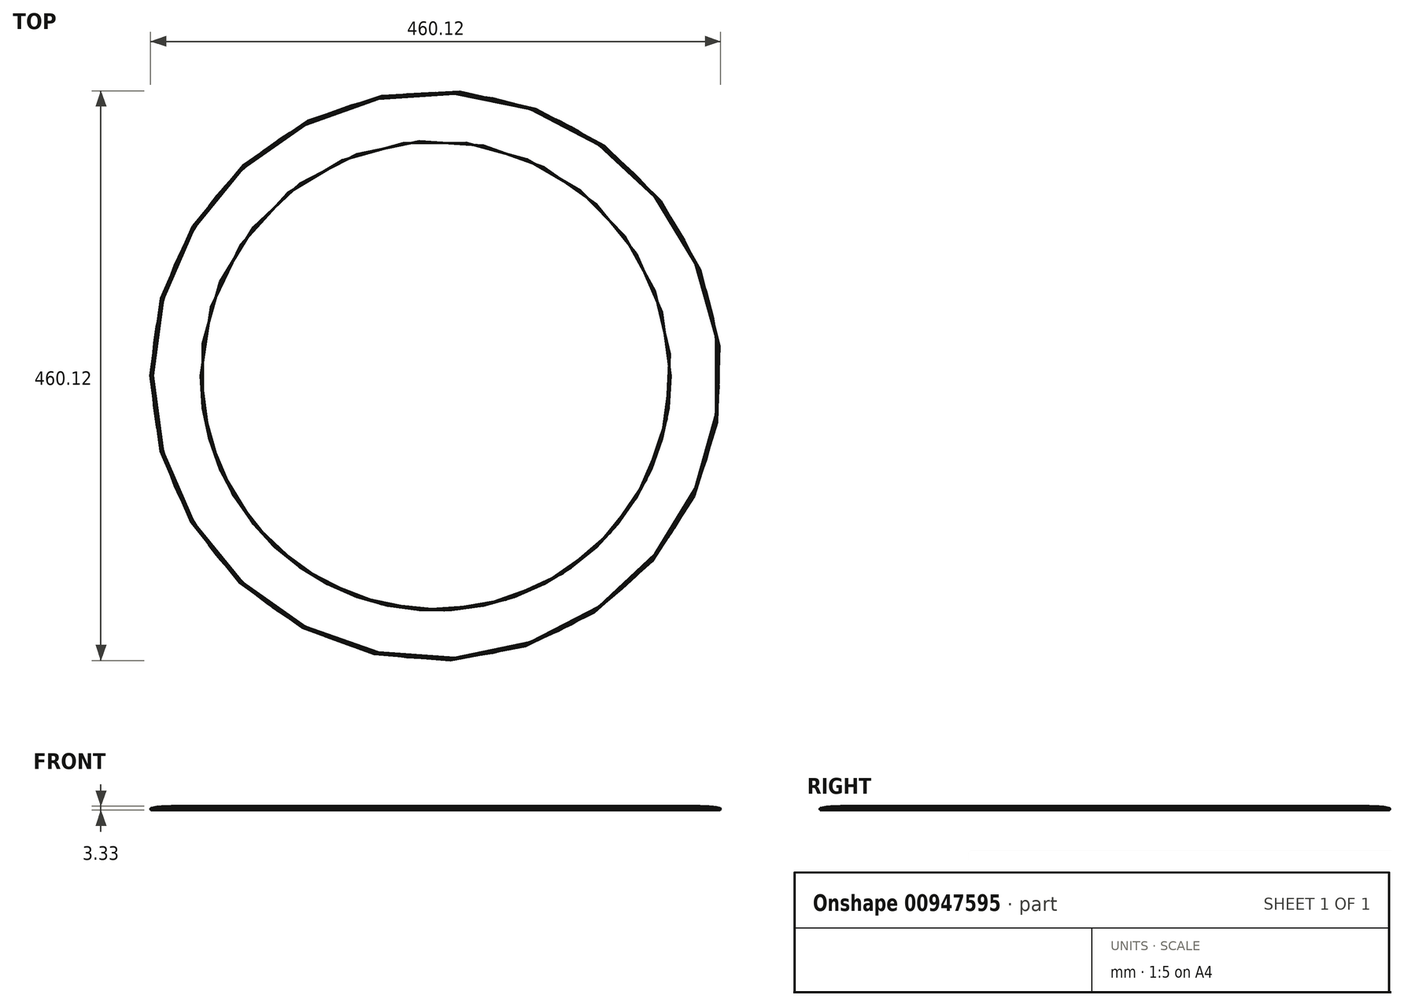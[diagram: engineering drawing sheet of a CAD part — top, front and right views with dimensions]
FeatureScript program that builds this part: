
annotation { "Feature Type Name" : "Feature", "Feature Type Description" : "" }
export const myFeature = defineFeature(function(context is Context, id is Id, definition is map)
    precondition{}
    {
        {
            var Q0;
            Q0=qCreatedBy(makeId("Front.planeOp"),FACE);
            var sketch = newSketch(context, id + "F0", { "sketchPlane" : qUnion([Q0])});
            skLineSegment(sketch, "E0", {"start": v(0, 0) * mm, "end": v(0, 158.75) * mm, "construction": true});
            skLineSegment(sketch, "E1", {"start": v(0, 0) * mm, "end": v(228.6, 0) * mm, "construction": true});
            skLineSegment(sketch, "E2", {"start": v(0, 158.75) * mm, "end": v(44.45, 158.75) * mm, "construction": true});
            skLineSegment(sketch, "E3", {"start": v(44.45, 158.75) * mm, "end": v(44.45, 143.35) * mm, "construction": true});
            skLineSegment(sketch, "E4", {"start": v(44.45, 158.75) * mm, "end": v(86, 158.75) * mm, "construction": true});
            skFitSpline(sketch, "E5", {"points": [v(86, 158.75) * mm, v(63.64, 148.01) * mm, v(44.45, 120.75) * mm, v(41.2, 74.17) * mm, v(59.88, 37.7) * mm, v(85.33, 18.53) * mm, v(127.5, 6.62) * mm, v(179.12, 3.65) * mm, v(188.03, 3.3) * mm, v(189.18, 2.94) * mm, v(189.55, 2.35) * mm, v(189.64, 2) * mm, v(188.74, 0) * mm], "startDerivative": vector(-219.08, -34.84) * mm, "endDerivative": vector(-71.32, -16.42) * mm});
            skPoint(sketch, "E6", {"position": v(65.23, 158.75) * mm});
            skFitSpline(sketch, "E7.MirrorCS", {"points": [v(-86, 158.75) * mm, v(-63.64, 148.01) * mm, v(-44.45, 120.75) * mm, v(-41.2, 74.17) * mm, v(-59.88, 37.7) * mm, v(-85.33, 18.53) * mm, v(-127.5, 6.62) * mm, v(-179.12, 3.65) * mm, v(-188.03, 3.3) * mm, v(-189.18, 2.94) * mm, v(-189.55, 2.35) * mm, v(-189.64, 2) * mm, v(-188.74, 0) * mm], "startDerivative": vector(219.08, -34.84) * mm, "endDerivative": vector(71.32, -16.42) * mm});
            skCircle(sketch, "E8", {"center": v(592.28, -587.42) * mm, "radius": 79.38 * mm});
            skFitSpline(sketch, "E9", {"points": [v(188.74, 0) * mm, v(142.2, 1) * mm, v(105.49, 6.94) * mm, v(70.12, 22.81) * mm, v(43.63, 55.57) * mm, v(36.1, 94.48) * mm, v(44.5, 129.14) * mm, v(58.85, 148.13) * mm, v(71.22, 156.88) * mm, v(74.26, 158.75) * mm, v(74.26, 158.75) * mm, v(86, 158.75) * mm], "startDerivative": vector(-370.06, -4.92) * mm, "endDerivative": vector(-42.57, -70.86) * mm});
            skLineSegment(sketch, "E10", {"start": v(53.68, 142.98) * mm, "end": v(56.49, 141.19) * mm});
            skFitSpline(sketch, "E11", {"points": [v(189.62, 1.7) * mm, v(189.8, 0.43) * mm, v(191.06, 0) * mm, v(226.52, 0) * mm, v(228.28, 0.2) * mm, v(228.4, 0.49) * mm, v(228.32, 1.15) * mm, v(227.18, 2) * mm, v(192.18, 3.05) * mm, v(190.01, 2.53) * mm, v(189.62, 1.7) * mm]});
            skCircle(sketch, "E12", {"center": v(229.22, 0.77) * mm, "radius": 0.84 * mm});
            skSolve(sketch);
        }
        {
            var Q0;
            Q0=makeQuery(id+"F0.imprint","IMPRINT",FACE,{"disambiguationData":[TD([[makeQuery(id+"F0.imprint","IMPRINT",EDGE,{"derivedFrom":sQuery(id+"F0.wireOp",EDGE,"E5")}),-1.0]])]});
            var Q1;
            Q1=sQuery(id+"F0.wireOp",EDGE,"E0");
            revolve(context, id + "F1", {"surfaceOperationType" : NewSurfaceOperationType.NEW, "entities" : qUnion([Q0]), "axis" : qUnion([Q1]), "revolveType" : RevolveType.FULL});
        }
        {
            var Q0;
            {var subQ0=sQuery(id+"F0.wireOp",EDGE,"E11");var subQ1=sQuery(id+"F0.wireOp",EDGE,"E5");var subQ2=makeQuery(id+"F0.imprint","INTERSECT",VERTEX,{"disambiguationData":[OD(0.0)],"derivedFrom":[subQ1,subQ0]});Q0=makeQuery(id+"F0.imprint","IMPRINT",FACE,{"disambiguationData":[TD([[makeQuery(id+"F0.imprint","IMPRINT",EDGE,{"disambiguationData":[TD([[subQ2,-1.0]])],"derivedFrom":subQ1}),1.0]])]});}
            var Q1;
            {var subQ0=sQuery(id+"F0.wireOp",EDGE,"E5");Q1=makeQuery(id+"F1.opRevolve","SWEPT_FACE",FACE,{"disambiguationData":[OSD([subQ0]),TDD([makeQuery(id+"F0.imprint","IMPRINT",EDGE,{"disambiguationData":[TD([[makeQuery(id+"F0.imprint","INTERSECT",VERTEX,{"derivedFrom":[subQ0,sQuery(id+"F0.wireOp",EDGE,"E10")]}),-1.0]])],"derivedFrom":subQ0})])]});}
            revolve(context, id + "F2", {"surfaceOperationType" : NewSurfaceOperationType.NEW, "entities" : qUnion([Q0]), "axis" : qUnion([Q1]), "revolveType" : RevolveType.FULL});
        }
        {
            var Q0;
            {var subQ0=sQuery(id+"F0.wireOp",EDGE,"E12");var subQ1=sQuery(id+"F0.wireOp",EDGE,"E11");var subQ2=makeQuery(id+"F0.imprint","INTERSECT",VERTEX,{"disambiguationData":[OD(0.0)],"derivedFrom":[subQ1,subQ0]});Q0=makeQuery(id+"F0.imprint","IMPRINT",FACE,{"disambiguationData":[TD([[makeQuery(id+"F0.imprint","IMPRINT",EDGE,{"disambiguationData":[TD([[subQ2,-1.0]])],"derivedFrom":subQ1}),-1.0]])]});}
            var Q1;
            Q1=sQuery(id+"F0.wireOp",EDGE,"E0");
            revolve(context, id + "F3", {"surfaceOperationType" : NewSurfaceOperationType.NEW, "entities" : qUnion([Q0]), "axis" : qUnion([Q1]), "revolveType" : RevolveType.FULL});
        }
    });
